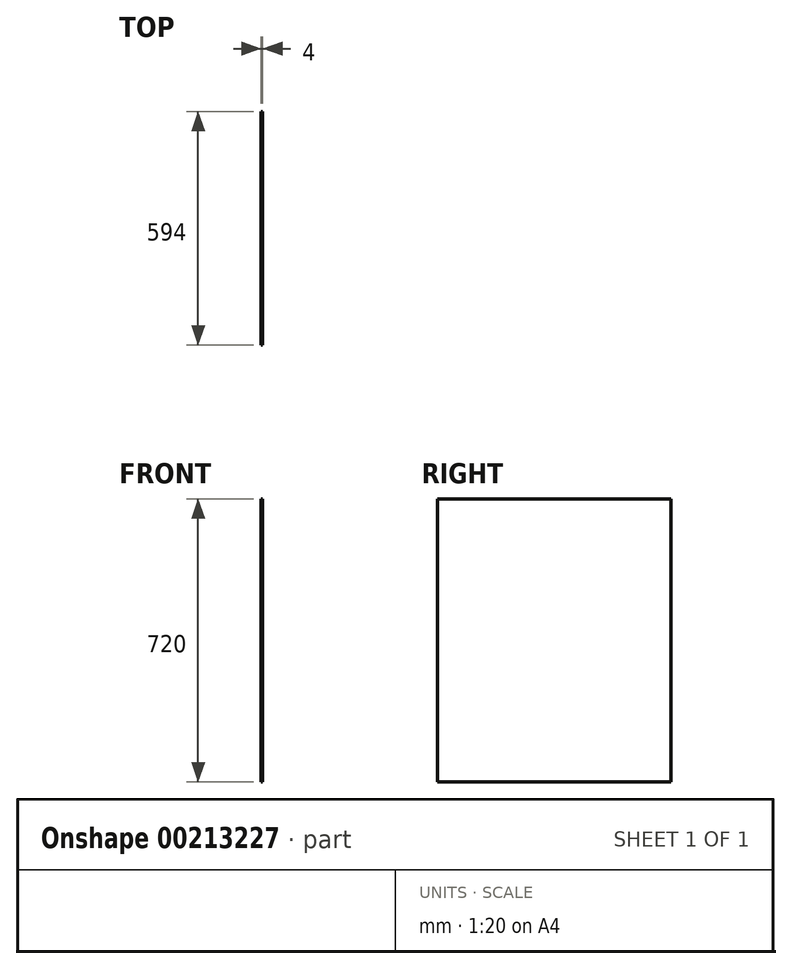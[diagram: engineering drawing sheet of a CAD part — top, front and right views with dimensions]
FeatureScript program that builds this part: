
annotation { "Feature Type Name" : "Feature", "Feature Type Description" : "" }
export const myFeature = defineFeature(function(context is Context, id is Id, definition is map)
    precondition{}
    {
        {
            var Q0;
            Q0=qCreatedBy(makeId("Right.planeOp"),FACE);
            var sketch = newSketch(context, id + "F0", { "sketchPlane" : qUnion([Q0])});
            skLineSegment(sketch, "E0.bottom", {"start": v(297, 360) * mm, "end": v(-297, 360) * mm});
            skLineSegment(sketch, "E0.top", {"start": v(297, -360) * mm, "end": v(-297, -360) * mm});
            skLineSegment(sketch, "E0.left", {"start": v(297, 360) * mm, "end": v(297, -360) * mm});
            skLineSegment(sketch, "E0.right", {"start": v(-297, 360) * mm, "end": v(-297, -360) * mm});
            skPoint(sketch, "E0.middle", {"position": v(0, 0) * mm});
            skSolve(sketch);
        }
        {
            var Q0;
            Q0=makeQuery(id+"F0.imprint","IMPRINT",FACE,{"disambiguationData":[TD([[makeQuery(id+"F0.imprint","IMPRINT",EDGE,{"derivedFrom":sQuery(id+"F0.wireOp",EDGE,"E0.bottom")}),1.0]])]});
            extrude(context, id + "F1", {"entities" : qUnion([Q0]), "endBound" : BoundingType.SYMMETRIC, "depth" : 4 * mm});
        }
    });
